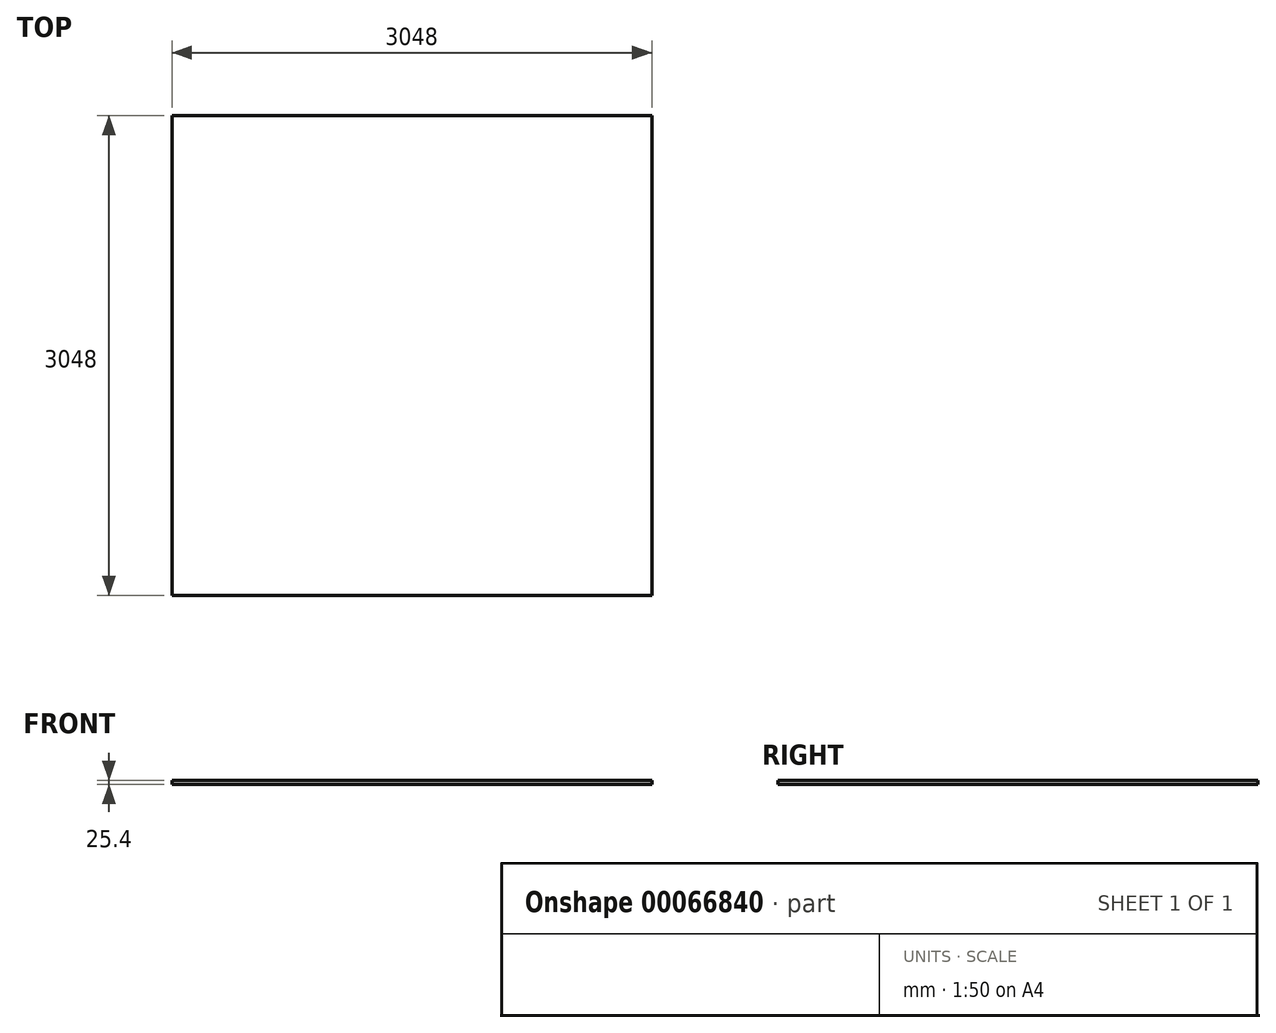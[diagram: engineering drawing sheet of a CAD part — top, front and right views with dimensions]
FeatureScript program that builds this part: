
annotation { "Feature Type Name" : "Feature", "Feature Type Description" : "" }
export const myFeature = defineFeature(function(context is Context, id is Id, definition is map)
    precondition{}
    {
        {
            var Q0;
            Q0=qCreatedBy(makeId("Top.planeOp"),FACE);
            var sketch = newSketch(context, id + "F0", { "sketchPlane" : qUnion([Q0])});
            skLineSegment(sketch, "E0.bottom", {"start": v(-1448.98, 1520.15) * mm, "end": v(1599.02, 1520.15) * mm});
            skLineSegment(sketch, "E0.top", {"start": v(-1448.98, -1527.85) * mm, "end": v(1599.02, -1527.85) * mm});
            skLineSegment(sketch, "E0.left", {"start": v(-1448.98, 1520.15) * mm, "end": v(-1448.98, -1527.85) * mm});
            skLineSegment(sketch, "E0.right", {"start": v(1599.02, 1520.15) * mm, "end": v(1599.02, -1527.85) * mm});
            skSolve(sketch);
        }
        {
            var Q0;
            Q0=makeQuery(id+"F0.imprint","IMPRINT",FACE,{"disambiguationData":[TD([[makeQuery(id+"F0.imprint","IMPRINT",EDGE,{"derivedFrom":sQuery(id+"F0.wireOp",EDGE,"E0.bottom")}),-1.0]])]});
            extrude(context, id + "F1", {"entities" : qUnion([Q0]), "depth" : 25.4 * mm});
        }
    });
